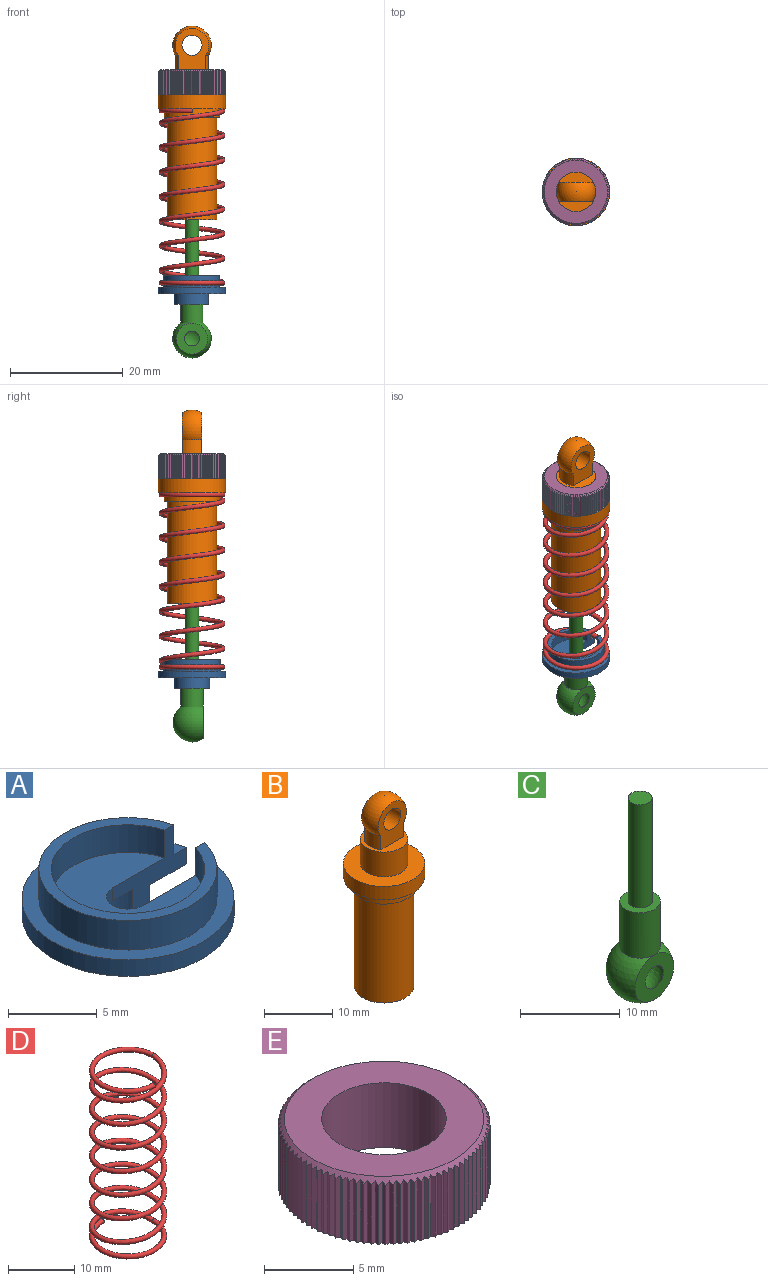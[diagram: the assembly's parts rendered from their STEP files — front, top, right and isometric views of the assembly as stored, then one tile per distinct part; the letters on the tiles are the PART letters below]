
ASSEMBLY  parts=5 mates=10
PART A: 14 faces, bbox 11.8x11.9x5.1 mm
  f0: cylinder r=1.21mm len=2.41mm, axis (0,0,1), area 3.4mm2, adj f3,f4,f12,f13
  f1: plane 10.03x9.89mm, normal (0,0,1), area 18.8mm2, adj f2,f11,f12,f13
  f2: cylinder r=4.32mm len=8.64mm, axis (0,0,1), area 47mm2, adj f1,f3,f12,f13
  f3: plane 8.64x8.46mm, normal (0,0,1), area 46mm2, adj f0,f2,f12,f13
  f4: plane 3.94x3.52mm, normal (0,0,-1), area 5.5mm2, adj f0,f5,f12,f13
  f5: cylinder r=1.97mm len=3.94mm, axis (0,0,1), area 22.3mm2, adj f4,f6,f12,f13
  f6: plane 6.35x6.11mm, normal (0,0,-1), area 16.5mm2, adj f5,f7,f12,f13
  f7: cylinder r=3.17mm len=6.35mm, axis (0,0,1), area 33.3mm2, adj f6,f8,f12,f13
  f8: plane 11.94x11.81mm, normal (0,0,-1), area 73.4mm2, adj f7,f9,f12,f13
  f9: cylinder r=5.97mm len=11.94mm, axis (0,0,1), area 40.1mm2, adj f8,f10,f12,f13
  f10: plane 11.94x11.81mm, normal (0,0,1), area 30.6mm2, adj f9,f11,f12,f13
  f11: cylinder r=5.02mm len=10.03mm, axis (0,0,1), area 59.1mm2, adj f1,f10,f12,f13
  f12: plane 5.85x5.08mm, normal (0,-1,0), area 10.7mm2, adj f0,f1,f2,f3,f4,f5,f6,f7
  f13: plane 5.85x5.08mm, normal (0,1,0), area 10.7mm2, adj f0,f1,f2,f3,f4,f5,f6,f7
PART B: 15 faces, bbox 11.9x11.9x34.3 mm
  f0: cylinder r=2.92mm len=3.43mm, axis (0,0,1), area 9.3mm2, adj f2,f6,f12,f13
  f1: cylinder r=2.92mm len=3.43mm, axis (0,0,1), area 9.3mm2, adj f2,f6,f12,f13
  f2: sphere r=3.43mm, area 50.6mm2, adj f0,f1,f12,f13
  f3: cylinder r=5.97mm len=11.94mm, axis (0,0,1), area 90.5mm2, adj f4,f11
  f4: plane 11.94x11.94mm, normal (0,0,1), area 73.6mm2, adj f3,f5
  f5: cylinder r=3.49mm len=6.99mm, axis (0,0,1), area 97.5mm2, adj f4,f6
  f6: plane 6.99x6.99mm, normal (0,0,1), area 19.5mm2, adj f0,f1,f5,f12,f13
  f7: plane 8.76x8.76mm, normal (0,0,-1), area 60.3mm2, adj f8
  f8: cylinder r=4.38mm len=18.16mm, axis (0,0,1), area 500mm2, adj f7,f9
  f9: plane 9.78x9.78mm, normal (0,0,-1), area 14.8mm2, adj f8,f10
  f10: cylinder r=4.89mm len=9.78mm, axis (0,0,1), area 46.8mm2, adj f9,f11
  f11: plane 11.94x11.94mm, normal (0,0,-1), area 36.8mm2, adj f3,f10
  f12: plane 7.31x5.94mm, normal (0,1,0), area 25.9mm2, adj f0,f1,f2,f6,f14
  f13: plane 7.31x5.94mm, normal (0,-1,0), area 25.9mm2, adj f0,f1,f2,f6,f14
  f14: cylinder r=1.78mm len=3.56mm, axis (0,-1,0), area 38.3mm2, adj f12,f13
PART C: 7 faces, bbox 6.9x6.9x24.5 mm
  f0: sphere r=3.43mm, area 103.3mm2, adj f1,f5
  f1: cylinder r=2.03mm len=5.59mm, axis (0,0,-1), area 71.3mm2, adj f0,f2
  f2: plane 4.06x4.06mm, normal (0,0,1), area 8.4mm2, adj f1,f3
  f3: cylinder r=1.21mm len=12.7mm, axis (0,0,-1), area 96.3mm2, adj f2,f4
  f4: plane 2.41x2.41mm, normal (0,0,1), area 4.6mm2, adj f3
  f5: plane 5.52x5.52mm, normal (0,-1,0), area 18.6mm2, adj f0,f6
  f6: sphere r=2.41mm, area 67.4mm2, adj f5
PART D: 5 faces, bbox 12.6x13.5x32 mm
  f0: bspline ~32x13.49mm, area 576.6mm2, adj f1,f3
  f1: torus R=5.46mm, axis (0,0,-1), area 61.6mm2, adj f0,f2
  f2: plane 0.76x0.76mm, normal (1,0,0), area 0.5mm2, adj f1
  f3: torus R=5.46mm, axis (0,0,1), area 61.6mm2, adj f0,f4
  f4: plane 0.76x0.76mm, normal (1,0,0), area 0.5mm2, adj f3
PART E: 184 faces, bbox 11.9x11.9x4.4 mm
  f0: plane 11.89x11.88mm, normal (0,0,-1), area 69.6mm2, adj f2,f4,f5,f6,f7,f8,f9,f10
  f1: cone r=5.97mm half-angle=45deg, axis (0,0,-1), area 13.9mm2, adj f3,f4,f5,f6,f7,f8,f9,f10
  f2: cylinder r=3.49mm len=6.99mm, axis (0,0,-1), area 97.5mm2, adj f0,f3
  f3: plane 11.18x11.18mm, normal (0,0,1), area 59.8mm2, adj f1,f2
  f4: plane 4.26x0.22mm, normal (-0.59,-0.81,0), area 1.1mm2, adj f0,f1,f5,f183
  f5: plane 4.26x0.19mm, normal (0.69,-0.72,0), area 1.1mm2, adj f0,f1,f4,f6
  f6: plane 4.26x0.23mm, normal (-0.53,-0.85,0), area 1.1mm2, adj f0,f1,f5,f7
  f7: plane 4.26x0.2mm, normal (0.74,-0.67,0), area 1.1mm2, adj f0,f1,f6,f8
  f8: plane 4.26x0.24mm, normal (-0.47,-0.88,0), area 1.1mm2, adj f0,f1,f7,f9
  f9: plane 4.26x0.21mm, normal (0.79,-0.62,0), area 1.1mm2, adj f0,f1,f8,f10
  f10: plane 4.26x0.24mm, normal (-0.41,-0.91,0), area 1.1mm2, adj f0,f1,f9,f11
  f11: plane 4.26x0.22mm, normal (0.83,-0.56,0), area 1.1mm2, adj f0,f1,f10,f12
  f12: plane 4.26x0.25mm, normal (-0.34,-0.94,0), area 1.1mm2, adj f0,f1,f11,f13
  f13: plane 4.26x0.23mm, normal (0.87,-0.5,0), area 1.1mm2, adj f0,f1,f12,f14
  f14: plane 4.26x0.26mm, normal (-0.27,-0.96,0), area 1.1mm2, adj f0,f1,f13,f15
  f15: plane 4.26x0.24mm, normal (0.9,-0.44,0), area 1.1mm2, adj f0,f1,f14,f16
  f16: plane 4.26x0.26mm, normal (-0.21,-0.98,0), area 1.1mm2, adj f0,f1,f15,f17
  f17: plane 4.26x0.25mm, normal (0.93,-0.38,0), area 1.1mm2, adj f0,f1,f16,f18
  f18: plane 4.26x0.26mm, normal (-0.14,-0.99,0), area 1.1mm2, adj f0,f1,f17,f19
  f19: plane 4.26x0.25mm, normal (0.95,-0.31,0), area 1.1mm2, adj f0,f1,f18,f20
  f20: plane 4.26x0.27mm, normal (-0.07,-1,0), area 1.1mm2, adj f0,f1,f19,f21
  f21: plane 4.26x0.26mm, normal (0.97,-0.24,0), area 1.1mm2, adj f0,f1,f20,f22
  f22: plane 4.26x0.27mm, normal (0,-1,0), area 1.1mm2, adj f0,f1,f21,f23
  f23: plane 4.26x0.26mm, normal (0.98,-0.18,0), area 1.1mm2, adj f0,f1,f22,f24
  f24: plane 4.26x0.27mm, normal (0.07,-1,0), area 1.1mm2, adj f0,f1,f23,f25
  f25: plane 4.26x0.27mm, normal (0.99,-0.11,0), area 1.1mm2, adj f0,f1,f24,f26
  f26: plane 4.26x0.26mm, normal (0.14,-0.99,0), area 1.1mm2, adj f0,f1,f25,f27
  f27: plane 4.26x0.27mm, normal (1,-0.04,0), area 1.1mm2, adj f0,f1,f26,f28
  f28: plane 4.26x0.26mm, normal (0.21,-0.98,0), area 1.1mm2, adj f0,f1,f27,f29
  f29: plane 4.26x0.27mm, normal (1,0.03,0), area 1.1mm2, adj f0,f1,f28,f30
  f30: plane 4.26x0.26mm, normal (0.28,-0.96,0), area 1.1mm2, adj f0,f1,f29,f31
  f31: plane 4.26x0.27mm, normal (0.99,0.1,0), area 1.1mm2, adj f0,f1,f30,f32
  f32: plane 4.26x0.25mm, normal (0.34,-0.94,0), area 1.1mm2, adj f0,f1,f31,f33
  f33: plane 4.26x0.26mm, normal (0.99,0.17,0), area 1.1mm2, adj f0,f1,f32,f34
  f34: plane 4.26x0.24mm, normal (0.41,-0.91,0), area 1.1mm2, adj f0,f1,f33,f35
  f35: plane 4.26x0.26mm, normal (0.97,0.24,0), area 1.1mm2, adj f0,f1,f34,f36
  f36: plane 4.26x0.24mm, normal (0.47,-0.88,0), area 1.1mm2, adj f0,f1,f35,f37
  f37: plane 4.26x0.25mm, normal (0.95,0.31,0), area 1.1mm2, adj f0,f1,f36,f38
  f38: plane 4.26x0.23mm, normal (0.53,-0.85,0), area 1.1mm2, adj f0,f1,f37,f39
  f39: plane 4.26x0.25mm, normal (0.93,0.37,0), area 1.1mm2, adj f0,f1,f38,f40
  f40: plane 4.26x0.22mm, normal (0.59,-0.81,0), area 1.1mm2, adj f0,f1,f39,f41
  f41: plane 4.26x0.24mm, normal (0.9,0.44,0), area 1.1mm2, adj f0,f1,f40,f42
  f42: plane 4.26x0.21mm, normal (0.64,-0.76,0), area 1.1mm2, adj f0,f1,f41,f43
  f43: plane 4.26x0.23mm, normal (0.87,0.5,0), area 1.1mm2, adj f0,f1,f42,f44
  f44: plane 4.26x0.19mm, normal (0.7,-0.72,0), area 1.1mm2, adj f0,f1,f43,f45
  f45: plane 4.26x0.22mm, normal (0.83,0.56,0), area 1.1mm2, adj f0,f1,f44,f46
  f46: plane 4.26x0.2mm, normal (0.74,-0.67,0), area 1.1mm2, adj f0,f1,f45,f47
  f47: plane 4.26x0.21mm, normal (0.79,0.61,0), area 1.1mm2, adj f0,f1,f46,f48
  f48: plane 4.26x0.21mm, normal (0.79,-0.61,0), area 1.1mm2, adj f0,f1,f47,f49
  f49: plane 4.26x0.2mm, normal (0.74,0.67,0), area 1.1mm2, adj f0,f1,f48,f50
  f50: plane 4.26x0.22mm, normal (0.83,-0.56,0), area 1.1mm2, adj f0,f1,f49,f51
  f51: plane 4.26x0.19mm, normal (0.7,0.72,0), area 1.1mm2, adj f0,f1,f50,f52
  f52: plane 4.26x0.23mm, normal (0.87,-0.5,0), area 1.1mm2, adj f0,f1,f51,f53
  f53: plane 4.26x0.21mm, normal (0.64,0.76,0), area 1.1mm2, adj f0,f1,f52,f54
  f54: plane 4.26x0.24mm, normal (0.9,-0.44,0), area 1.1mm2, adj f0,f1,f53,f55
  f55: plane 4.26x0.22mm, normal (0.59,0.81,0), area 1.1mm2, adj f0,f1,f54,f56
  f56: plane 4.26x0.25mm, normal (0.93,-0.37,0), area 1.1mm2, adj f0,f1,f55,f57
  f57: plane 4.26x0.23mm, normal (0.53,0.85,0), area 1.1mm2, adj f0,f1,f56,f58
  f58: plane 4.26x0.25mm, normal (0.95,-0.31,0), area 1.1mm2, adj f0,f1,f57,f59
  f59: plane 4.26x0.24mm, normal (0.47,0.88,0), area 1.1mm2, adj f0,f1,f58,f60
  f60: plane 4.26x0.26mm, normal (0.97,-0.24,0), area 1.1mm2, adj f0,f1,f59,f61
  f61: plane 4.26x0.24mm, normal (0.41,0.91,0), area 1.1mm2, adj f0,f1,f60,f62
  f62: plane 4.26x0.26mm, normal (0.99,-0.17,0), area 1.1mm2, adj f0,f1,f61,f63
  f63: plane 4.26x0.25mm, normal (0.34,0.94,0), area 1.1mm2, adj f0,f1,f62,f64
  f64: plane 4.26x0.27mm, normal (0.99,-0.1,0), area 1.1mm2, adj f0,f1,f63,f65
  f65: plane 4.26x0.26mm, normal (0.28,0.96,0), area 1.1mm2, adj f0,f1,f64,f66
  f66: plane 4.26x0.27mm, normal (1,-0.03,0), area 1.1mm2, adj f0,f1,f65,f67
  f67: plane 4.26x0.26mm, normal (0.21,0.98,0), area 1.1mm2, adj f0,f1,f66,f68
  f68: plane 4.26x0.27mm, normal (1,0.04,0), area 1.1mm2, adj f0,f1,f67,f69
  f69: plane 4.26x0.26mm, normal (0.14,0.99,0), area 1.1mm2, adj f0,f1,f68,f70
  f70: plane 4.26x0.27mm, normal (0.99,0.11,0), area 1.1mm2, adj f0,f1,f69,f71
  f71: plane 4.26x0.27mm, normal (0.07,1,0), area 1.1mm2, adj f0,f1,f70,f72
  f72: plane 4.26x0.26mm, normal (0.98,0.18,0), area 1.1mm2, adj f0,f1,f71,f73
  f73: plane 4.26x0.27mm, normal (0,1,0), area 1.1mm2, adj f0,f1,f72,f74
  f74: plane 4.26x0.26mm, normal (0.97,0.24,0), area 1.1mm2, adj f0,f1,f73,f75
  f75: plane 4.26x0.27mm, normal (-0.07,1,0), area 1.1mm2, adj f0,f1,f74,f76
  f76: plane 4.26x0.25mm, normal (0.95,0.31,0), area 1.1mm2, adj f0,f1,f75,f77
  f77: plane 4.26x0.26mm, normal (-0.14,0.99,0), area 1.1mm2, adj f0,f1,f76,f78
  f78: plane 4.26x0.25mm, normal (0.93,0.38,0), area 1.1mm2, adj f0,f1,f77,f79
  f79: plane 4.26x0.26mm, normal (-0.21,0.98,0), area 1.1mm2, adj f0,f1,f78,f80
  f80: plane 4.26x0.24mm, normal (0.9,0.44,0), area 1.1mm2, adj f0,f1,f79,f81
  f81: plane 4.26x0.26mm, normal (-0.27,0.96,0), area 1.1mm2, adj f0,f1,f80,f82
  f82: plane 4.26x0.23mm, normal (0.87,0.5,0), area 1.1mm2, adj f0,f1,f81,f83
  f83: plane 4.26x0.25mm, normal (-0.34,0.94,0), area 1.1mm2, adj f0,f1,f82,f84
  f84: plane 4.26x0.22mm, normal (0.83,0.56,0), area 1.1mm2, adj f0,f1,f83,f85
  f85: plane 4.26x0.24mm, normal (-0.41,0.91,0), area 1.1mm2, adj f0,f1,f84,f86
  f86: plane 4.26x0.21mm, normal (0.79,0.62,0), area 1.1mm2, adj f0,f1,f85,f87
  f87: plane 4.26x0.24mm, normal (-0.47,0.88,0), area 1.1mm2, adj f0,f1,f86,f88
  f88: plane 4.26x0.2mm, normal (0.74,0.67,0), area 1.1mm2, adj f0,f1,f87,f89
  f89: plane 4.26x0.23mm, normal (-0.53,0.85,0), area 1.1mm2, adj f0,f1,f88,f90
  f90: plane 4.26x0.19mm, normal (0.69,0.72,0), area 1.1mm2, adj f0,f1,f89,f91
  f91: plane 4.26x0.22mm, normal (-0.59,0.81,0), area 1.1mm2, adj f0,f1,f90,f92
  f92: plane 4.26x0.21mm, normal (0.64,0.77,0), area 1.1mm2, adj f0,f1,f91,f93
  f93: plane 4.26x0.21mm, normal (-0.64,0.77,0), area 1.1mm2, adj f0,f1,f92,f94
  f94: plane 4.26x0.22mm, normal (0.59,0.81,0), area 1.1mm2, adj f0,f1,f93,f95
  f95: plane 4.26x0.19mm, normal (-0.69,0.72,0), area 1.1mm2, adj f0,f1,f94,f96
  f96: plane 4.26x0.23mm, normal (0.53,0.85,0), area 1.1mm2, adj f0,f1,f95,f97
  f97: plane 4.26x0.2mm, normal (-0.74,0.67,0), area 1.1mm2, adj f0,f1,f96,f98
  f98: plane 4.26x0.24mm, normal (0.47,0.88,0), area 1.1mm2, adj f0,f1,f97,f99
  f99: plane 4.26x0.21mm, normal (-0.79,0.62,0), area 1.1mm2, adj f0,f1,f98,f100
  f100: plane 4.26x0.24mm, normal (0.41,0.91,0), area 1.1mm2, adj f0,f1,f99,f101
  f101: plane 4.26x0.22mm, normal (-0.83,0.56,0), area 1.1mm2, adj f0,f1,f100,f102
  f102: plane 4.26x0.25mm, normal (0.34,0.94,0), area 1.1mm2, adj f0,f1,f101,f103
  f103: plane 4.26x0.23mm, normal (-0.87,0.5,0), area 1.1mm2, adj f0,f1,f102,f104
  f104: plane 4.26x0.26mm, normal (0.27,0.96,0), area 1.1mm2, adj f0,f1,f103,f105
  f105: plane 4.26x0.24mm, normal (-0.9,0.44,0), area 1.1mm2, adj f0,f1,f104,f106
  f106: plane 4.26x0.26mm, normal (0.21,0.98,0), area 1.1mm2, adj f0,f1,f105,f107
  f107: plane 4.26x0.25mm, normal (-0.93,0.38,0), area 1.1mm2, adj f0,f1,f106,f108
  f108: plane 4.26x0.26mm, normal (0.14,0.99,0), area 1.1mm2, adj f0,f1,f107,f109
  f109: plane 4.26x0.25mm, normal (-0.95,0.31,0), area 1.1mm2, adj f0,f1,f108,f110
  f110: plane 4.26x0.27mm, normal (0.07,1,0), area 1.1mm2, adj f0,f1,f109,f111
  f111: plane 4.26x0.26mm, normal (-0.97,0.24,0), area 1.1mm2, adj f0,f1,f110,f112
  f112: plane 4.26x0.27mm, normal (0,1,0), area 1.1mm2, adj f0,f1,f111,f113
  f113: plane 4.26x0.26mm, normal (-0.98,0.18,0), area 1.1mm2, adj f0,f1,f112,f114
  f114: plane 4.26x0.27mm, normal (-0.07,1,0), area 1.1mm2, adj f0,f1,f113,f115
  f115: plane 4.26x0.27mm, normal (-0.99,0.11,0), area 1.1mm2, adj f0,f1,f114,f116
  f116: plane 4.26x0.26mm, normal (-0.14,0.99,0), area 1.1mm2, adj f0,f1,f115,f117
  f117: plane 4.26x0.27mm, normal (-1,0.04,0), area 1.1mm2, adj f0,f1,f116,f118
  f118: plane 4.26x0.26mm, normal (-0.21,0.98,0), area 1.1mm2, adj f0,f1,f117,f119
  f119: plane 4.26x0.27mm, normal (-1,-0.03,0), area 1.1mm2, adj f0,f1,f118,f120
  f120: plane 4.26x0.26mm, normal (-0.28,0.96,0), area 1.1mm2, adj f0,f1,f119,f121
  f121: plane 4.26x0.27mm, normal (-0.99,-0.1,0), area 1.1mm2, adj f0,f1,f120,f122
  f122: plane 4.26x0.25mm, normal (-0.34,0.94,0), area 1.1mm2, adj f0,f1,f121,f123
  f123: plane 4.26x0.26mm, normal (-0.99,-0.17,0), area 1.1mm2, adj f0,f1,f122,f124
  f124: plane 4.26x0.24mm, normal (-0.41,0.91,0), area 1.1mm2, adj f0,f1,f123,f125
  f125: plane 4.26x0.26mm, normal (-0.97,-0.24,0), area 1.1mm2, adj f0,f1,f124,f126
  f126: plane 4.26x0.24mm, normal (-0.47,0.88,0), area 1.1mm2, adj f0,f1,f125,f127
  f127: plane 4.26x0.25mm, normal (-0.95,-0.31,0), area 1.1mm2, adj f0,f1,f126,f128
  f128: plane 4.26x0.23mm, normal (-0.53,0.85,0), area 1.1mm2, adj f0,f1,f127,f129
  f129: plane 4.26x0.25mm, normal (-0.93,-0.37,0), area 1.1mm2, adj f0,f1,f128,f130
  f130: plane 4.26x0.22mm, normal (-0.59,0.81,0), area 1.1mm2, adj f0,f1,f129,f131
  f131: plane 4.26x0.24mm, normal (-0.9,-0.44,0), area 1.1mm2, adj f0,f1,f130,f132
  f132: plane 4.26x0.21mm, normal (-0.64,0.76,0), area 1.1mm2, adj f0,f1,f131,f133
  f133: plane 4.26x0.23mm, normal (-0.87,-0.5,0), area 1.1mm2, adj f0,f1,f132,f134
  f134: plane 4.26x0.19mm, normal (-0.7,0.72,0), area 1.1mm2, adj f0,f1,f133,f135
  f135: plane 4.26x0.22mm, normal (-0.83,-0.56,0), area 1.1mm2, adj f0,f1,f134,f136
  f136: plane 4.26x0.2mm, normal (-0.74,0.67,0), area 1.1mm2, adj f0,f1,f135,f137
  f137: plane 4.26x0.21mm, normal (-0.79,-0.61,0), area 1.1mm2, adj f0,f1,f136,f138
  f138: plane 4.26x0.21mm, normal (-0.79,0.61,0), area 1.1mm2, adj f0,f1,f137,f139
  f139: plane 4.26x0.2mm, normal (-0.74,-0.67,0), area 1.1mm2, adj f0,f1,f138,f140
  f140: plane 4.26x0.22mm, normal (-0.83,0.56,0), area 1.1mm2, adj f0,f1,f139,f141
  f141: plane 4.26x0.19mm, normal (-0.7,-0.72,0), area 1.1mm2, adj f0,f1,f140,f142
  f142: plane 4.26x0.23mm, normal (-0.87,0.5,0), area 1.1mm2, adj f0,f1,f141,f143
  f143: plane 4.26x0.21mm, normal (-0.64,-0.76,0), area 1.1mm2, adj f0,f1,f142,f144
  f144: plane 4.26x0.24mm, normal (-0.9,0.44,0), area 1.1mm2, adj f0,f1,f143,f145
  f145: plane 4.26x0.22mm, normal (-0.59,-0.81,0), area 1.1mm2, adj f0,f1,f144,f146
  f146: plane 4.26x0.25mm, normal (-0.93,0.37,0), area 1.1mm2, adj f0,f1,f145,f147
  f147: plane 4.26x0.23mm, normal (-0.53,-0.85,0), area 1.1mm2, adj f0,f1,f146,f148
  f148: plane 4.26x0.25mm, normal (-0.95,0.31,0), area 1.1mm2, adj f0,f1,f147,f149
  f149: plane 4.26x0.24mm, normal (-0.47,-0.88,0), area 1.1mm2, adj f0,f1,f148,f150
  f150: plane 4.26x0.26mm, normal (-0.97,0.24,0), area 1.1mm2, adj f0,f1,f149,f151
  f151: plane 4.26x0.24mm, normal (-0.41,-0.91,0), area 1.1mm2, adj f0,f1,f150,f152
  f152: plane 4.26x0.26mm, normal (-0.99,0.17,0), area 1.1mm2, adj f0,f1,f151,f153
  f153: plane 4.26x0.25mm, normal (-0.34,-0.94,0), area 1.1mm2, adj f0,f1,f152,f154
  f154: plane 4.26x0.27mm, normal (-0.99,0.1,0), area 1.1mm2, adj f0,f1,f153,f155
  f155: plane 4.26x0.26mm, normal (-0.28,-0.96,0), area 1.1mm2, adj f0,f1,f154,f156
  f156: plane 4.26x0.27mm, normal (-1,0.03,0), area 1.1mm2, adj f0,f1,f155,f157
  f157: plane 4.26x0.26mm, normal (-0.21,-0.98,0), area 1.1mm2, adj f0,f1,f156,f158
  f158: plane 4.26x0.27mm, normal (-1,-0.04,0), area 1.1mm2, adj f0,f1,f157,f159
  f159: plane 4.26x0.26mm, normal (-0.14,-0.99,0), area 1.1mm2, adj f0,f1,f158,f160
  f160: plane 4.26x0.27mm, normal (-0.99,-0.11,0), area 1.1mm2, adj f0,f1,f159,f161
  f161: plane 4.26x0.27mm, normal (-0.07,-1,0), area 1.1mm2, adj f0,f1,f160,f162
  f162: plane 4.26x0.26mm, normal (-0.98,-0.18,0), area 1.1mm2, adj f0,f1,f161,f163
  f163: plane 4.26x0.27mm, normal (0,-1,0), area 1.1mm2, adj f0,f1,f162,f164
  f164: plane 4.26x0.26mm, normal (-0.97,-0.24,0), area 1.1mm2, adj f0,f1,f163,f165
  f165: plane 4.26x0.27mm, normal (0.07,-1,0), area 1.1mm2, adj f0,f1,f164,f166
  f166: plane 4.26x0.25mm, normal (-0.95,-0.31,0), area 1.1mm2, adj f0,f1,f165,f167
  f167: plane 4.26x0.26mm, normal (0.14,-0.99,0), area 1.1mm2, adj f0,f1,f166,f168
  f168: plane 4.26x0.25mm, normal (-0.93,-0.38,0), area 1.1mm2, adj f0,f1,f167,f169
  f169: plane 4.26x0.26mm, normal (0.21,-0.98,0), area 1.1mm2, adj f0,f1,f168,f170
  f170: plane 4.26x0.24mm, normal (-0.9,-0.44,0), area 1.1mm2, adj f0,f1,f169,f171
  f171: plane 4.26x0.26mm, normal (0.27,-0.96,0), area 1.1mm2, adj f0,f1,f170,f172
  f172: plane 4.26x0.23mm, normal (-0.87,-0.5,0), area 1.1mm2, adj f0,f1,f171,f173
  f173: plane 4.26x0.25mm, normal (0.34,-0.94,0), area 1.1mm2, adj f0,f1,f172,f174
  f174: plane 4.26x0.22mm, normal (-0.83,-0.56,0), area 1.1mm2, adj f0,f1,f173,f175
  f175: plane 4.26x0.24mm, normal (0.41,-0.91,0), area 1.1mm2, adj f0,f1,f174,f176
  f176: plane 4.26x0.21mm, normal (-0.79,-0.62,0), area 1.1mm2, adj f0,f1,f175,f177
  f177: plane 4.26x0.24mm, normal (0.47,-0.88,0), area 1.1mm2, adj f0,f1,f176,f178
  f178: plane 4.26x0.2mm, normal (-0.74,-0.67,0), area 1.1mm2, adj f0,f1,f177,f179
  f179: plane 4.26x0.23mm, normal (0.53,-0.85,0), area 1.1mm2, adj f0,f1,f178,f180
  f180: plane 4.26x0.19mm, normal (-0.69,-0.72,0), area 1.1mm2, adj f0,f1,f179,f181
  f181: plane 4.26x0.22mm, normal (0.59,-0.81,0), area 1.1mm2, adj f0,f1,f180,f182
  f182: plane 4.26x0.21mm, normal (-0.64,-0.77,0), area 1.1mm2, adj f0,f1,f181,f183
  f183: plane 4.26x0.21mm, normal (0.64,-0.77,0), area 1.1mm2, adj f0,f1,f4,f182
PLACE A t=(-6.56,1.2,-22.41)mm
PLACE B t=(-6.56,1.2,-7.43)mm
PLACE C t=(-6.56,1.2,-25.72)mm
PLACE D t=(-6.56,1.2,-18.6)mm
PLACE E t=(-6.56,1.2,14.67)mm
MATE cylindrical C.f1 <-> B.f0  axis (0,0,-1) through (-6.56,1.2,-13.78)mm
MATE planar A.f4 <-> C.f1  axis (0,0,-1) through (-6.56,2.4,-20.13)mm
MATE parallel C.f5 <-> B.f13  axis (0,-1,0) through (-6.56,-0.84,-28.48)mm
MATE cylindrical E.f1 <-> B.f0  axis (0,0,-1) through (-6.56,1.2,19.11)mm
MATE cylindrical D.f1 <-> B.f0  axis (0,0,-1) through (-6.56,1.2,11.88)mm
MATE parallel A.f12 <-> C.f5  axis (0,-1,0) through (-2.41,2.4,-19.24)mm
MATE planar E.f1 <-> B.f0  axis (0,0,-1) through (-6.56,1.2,14.67)mm
MATE cylindrical A.f0 <-> C.f1  axis (0,0,1) through (-6.56,1.2,-21.27)mm
MATE planar C.f1 <-> B.f0  axis (0,0,1) through (-6.56,1.2,-7.43)mm
MATE planar D.f1 <-> B.f0  axis (0,0,-1) through (-6.56,1.2,11.88)mm
